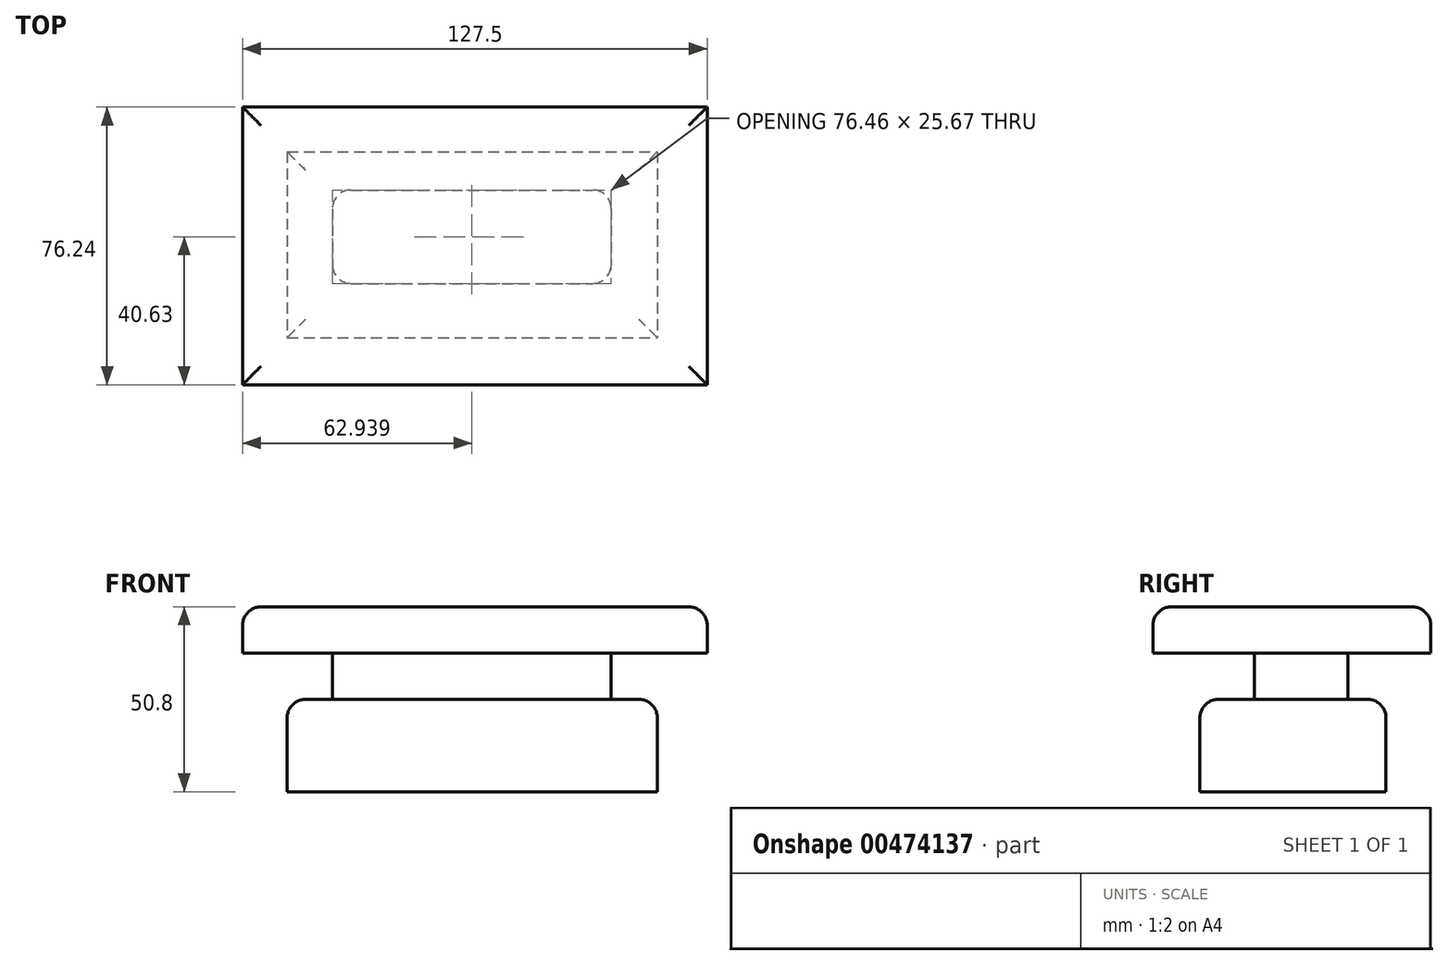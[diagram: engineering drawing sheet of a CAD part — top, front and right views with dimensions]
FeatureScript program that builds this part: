
annotation { "Feature Type Name" : "Feature", "Feature Type Description" : "" }
export const myFeature = defineFeature(function(context is Context, id is Id, definition is map)
    precondition{}
    {
        {
            var Q0;
            Q0=qCreatedBy(makeId("Top.planeOp"),FACE);
            var sketch = newSketch(context, id + "F0", { "sketchPlane" : qUnion([Q0])});
            skLineSegment(sketch, "E0.bottom", {"start": v(-65.14, 19.54) * mm, "end": v(36.45, 19.54) * mm});
            skLineSegment(sketch, "E0.top", {"start": v(-65.14, -31.52) * mm, "end": v(36.45, -31.52) * mm});
            skLineSegment(sketch, "E0.left", {"start": v(-65.14, 19.54) * mm, "end": v(-65.14, -31.52) * mm});
            skLineSegment(sketch, "E0.right", {"start": v(36.45, 19.54) * mm, "end": v(36.45, -31.52) * mm});
            skSolve(sketch);
        }
        {
            var Q0;
            Q0=makeQuery(id+"F0.imprint","IMPRINT",FACE,{"disambiguationData":[TD([[makeQuery(id+"F0.imprint","IMPRINT",EDGE,{"derivedFrom":sQuery(id+"F0.wireOp",EDGE,"E0.bottom")}),-1.0]])]});
            extrude(context, id + "F1", {"entities" : qUnion([Q0]), "depth" : 25.4 * mm});
        }
        {
            var Q0;
            Q0=makeQuery(id+"F1.opExtrude","CAP_EDGE",EDGE,{"disambiguationData":[OSD([sQuery(id+"F0.wireOp",EDGE,"E0.top")])],"isStart":false});
            var Q1;
            Q1=makeQuery(id+"F1.opExtrude","CAP_EDGE",EDGE,{"disambiguationData":[OSD([sQuery(id+"F0.wireOp",EDGE,"E0.left")])],"isStart":false});
            var Q2;
            Q2=makeQuery(id+"F1.opExtrude","CAP_EDGE",EDGE,{"disambiguationData":[OSD([sQuery(id+"F0.wireOp",EDGE,"E0.bottom")])],"isStart":false});
            var Q3;
            Q3=makeQuery(id+"F1.opExtrude","CAP_EDGE",EDGE,{"disambiguationData":[OSD([sQuery(id+"F0.wireOp",EDGE,"E0.right")])],"isStart":false});
            fillet(context, id + "F2", {"entities" : qUnion([Q0, Q1, Q2, Q3]), "radius" : 5.08 * mm, "tangentPropagation" : true, "allowEdgeOverflow" : false});
        }
        {
            var Q0;
            Q0=makeQuery(id+"F1.opExtrude","CAP_FACE",FACE,{"disambiguationData":[OSD([sQuery(id+"F0.wireOp",EDGE,"E0.bottom"),sQuery(id+"F0.wireOp",EDGE,"E0.top"),sQuery(id+"F0.wireOp",EDGE,"E0.left"),sQuery(id+"F0.wireOp",EDGE,"E0.right")])],"isStart":false});
            var sketch = newSketch(context, id + "F3", { "sketchPlane" : qUnion([Q0])});
            skLineSegment(sketch, "E1.bottom", {"start": v(-52.67, 9.04) * mm, "end": v(23.8, 9.04) * mm});
            skLineSegment(sketch, "E1.top", {"start": v(-52.67, -16.62) * mm, "end": v(23.8, -16.62) * mm});
            skLineSegment(sketch, "E1.left", {"start": v(-52.67, 9.04) * mm, "end": v(-52.67, -16.62) * mm});
            skLineSegment(sketch, "E1.right", {"start": v(23.8, 9.04) * mm, "end": v(23.8, -16.62) * mm});
            skSolve(sketch);
        }
        {
            var Q0;
            Q0=makeQuery(id+"F3.imprint","IMPRINT",FACE,{"disambiguationData":[TD([[makeQuery(id+"F3.imprint","IMPRINT",EDGE,{"derivedFrom":sQuery(id+"F3.wireOp",EDGE,"E1.bottom")}),-1.0]])]});
            extrude(context, id + "F4", {"entities" : qUnion([Q0]), "operationType" : NewBodyOperationType.ADD, "depth" : 12.7 * mm});
        }
        {
            var Q0;
            Q0=makeQuery(id+"F4.opExtrude","SWEPT_EDGE",EDGE,{"disambiguationData":[OSD([sQuery(id+"F3.wireOp",EDGE,"E1.top"),sQuery(id+"F3.wireOp",EDGE,"E1.left")])]});
            var Q1;
            Q1=makeQuery(id+"F4.opExtrude","SWEPT_EDGE",EDGE,{"disambiguationData":[OSD([sQuery(id+"F3.wireOp",EDGE,"E1.top"),sQuery(id+"F3.wireOp",EDGE,"E1.right")])]});
            var Q2;
            Q2=makeQuery(id+"F4.opExtrude","SWEPT_EDGE",EDGE,{"disambiguationData":[OSD([sQuery(id+"F3.wireOp",EDGE,"E1.bottom"),sQuery(id+"F3.wireOp",EDGE,"E1.left")])]});
            var Q3;
            Q3=makeQuery(id+"F4.opExtrude","SWEPT_EDGE",EDGE,{"disambiguationData":[OSD([sQuery(id+"F3.wireOp",EDGE,"E1.bottom"),sQuery(id+"F3.wireOp",EDGE,"E1.right")])]});
            fillet(context, id + "F5", {"entities" : qUnion([Q0, Q1, Q2, Q3]), "radius" : 5.08 * mm, "tangentPropagation" : true, "allowEdgeOverflow" : false});
        }
        {
            var Q0;
            Q0=makeQuery(id+"F4.opExtrude","CAP_FACE",FACE,{"disambiguationData":[OSD([sQuery(id+"F3.wireOp",EDGE,"E1.bottom"),sQuery(id+"F3.wireOp",EDGE,"E1.top"),sQuery(id+"F3.wireOp",EDGE,"E1.left"),sQuery(id+"F3.wireOp",EDGE,"E1.right")])],"isStart":false});
            var sketch = newSketch(context, id + "F6", { "sketchPlane" : qUnion([Q0])});
            skLineSegment(sketch, "E2.bottom", {"start": v(-77.38, 31.82) * mm, "end": v(50.12, 31.82) * mm});
            skLineSegment(sketch, "E2.top", {"start": v(-77.38, -44.42) * mm, "end": v(50.12, -44.42) * mm});
            skLineSegment(sketch, "E2.left", {"start": v(-77.38, 31.82) * mm, "end": v(-77.38, -44.42) * mm});
            skLineSegment(sketch, "E2.right", {"start": v(50.12, 31.82) * mm, "end": v(50.12, -44.42) * mm});
            skSolve(sketch);
        }
        {
            var Q0;
            Q0=makeQuery(id+"F6.imprint","IMPRINT",FACE,{"disambiguationData":[TD([[makeQuery(id+"F6.imprint","IMPRINT",EDGE,{"derivedFrom":sQuery(id+"F6.wireOp",EDGE,"E2.bottom")}),-1.0]])]});
            var Q1;
            {var subQ3=sQuery(id+"F3.wireOp",EDGE,"E1.bottom");Q1=makeQuery(id+"F6.imprint","IMPRINT",FACE,{"disambiguationData":[TD([[makeQuery(id+"F6.imprint","IMPRINT",EDGE,{"derivedFrom":makeQuery(id+"F4.opExtrude","CAP_EDGE",EDGE,{"disambiguationData":[OSD([subQ3])],"isStart":false})}),-1.0]])]});}
            extrude(context, id + "F7", {"entities" : qUnion([Q0, Q1]), "operationType" : NewBodyOperationType.ADD, "depth" : 12.7 * mm});
        }
        {
            var Q0;
            Q0=makeQuery(id+"F7.opExtrude","CAP_EDGE",EDGE,{"disambiguationData":[OSD([sQuery(id+"F6.wireOp",EDGE,"E2.top")])],"isStart":false});
            var Q1;
            Q1=makeQuery(id+"F7.opExtrude","CAP_EDGE",EDGE,{"disambiguationData":[OSD([sQuery(id+"F6.wireOp",EDGE,"E2.left")])],"isStart":false});
            var Q2;
            Q2=makeQuery(id+"F7.opExtrude","CAP_EDGE",EDGE,{"disambiguationData":[OSD([sQuery(id+"F6.wireOp",EDGE,"E2.bottom")])],"isStart":false});
            var Q3;
            Q3=makeQuery(id+"F7.opExtrude","CAP_EDGE",EDGE,{"disambiguationData":[OSD([sQuery(id+"F6.wireOp",EDGE,"E2.right")])],"isStart":false});
            fillet(context, id + "F8", {"entities" : qUnion([Q0, Q1, Q2, Q3]), "radius" : 5.08 * mm, "tangentPropagation" : true, "allowEdgeOverflow" : false});
        }
    });
